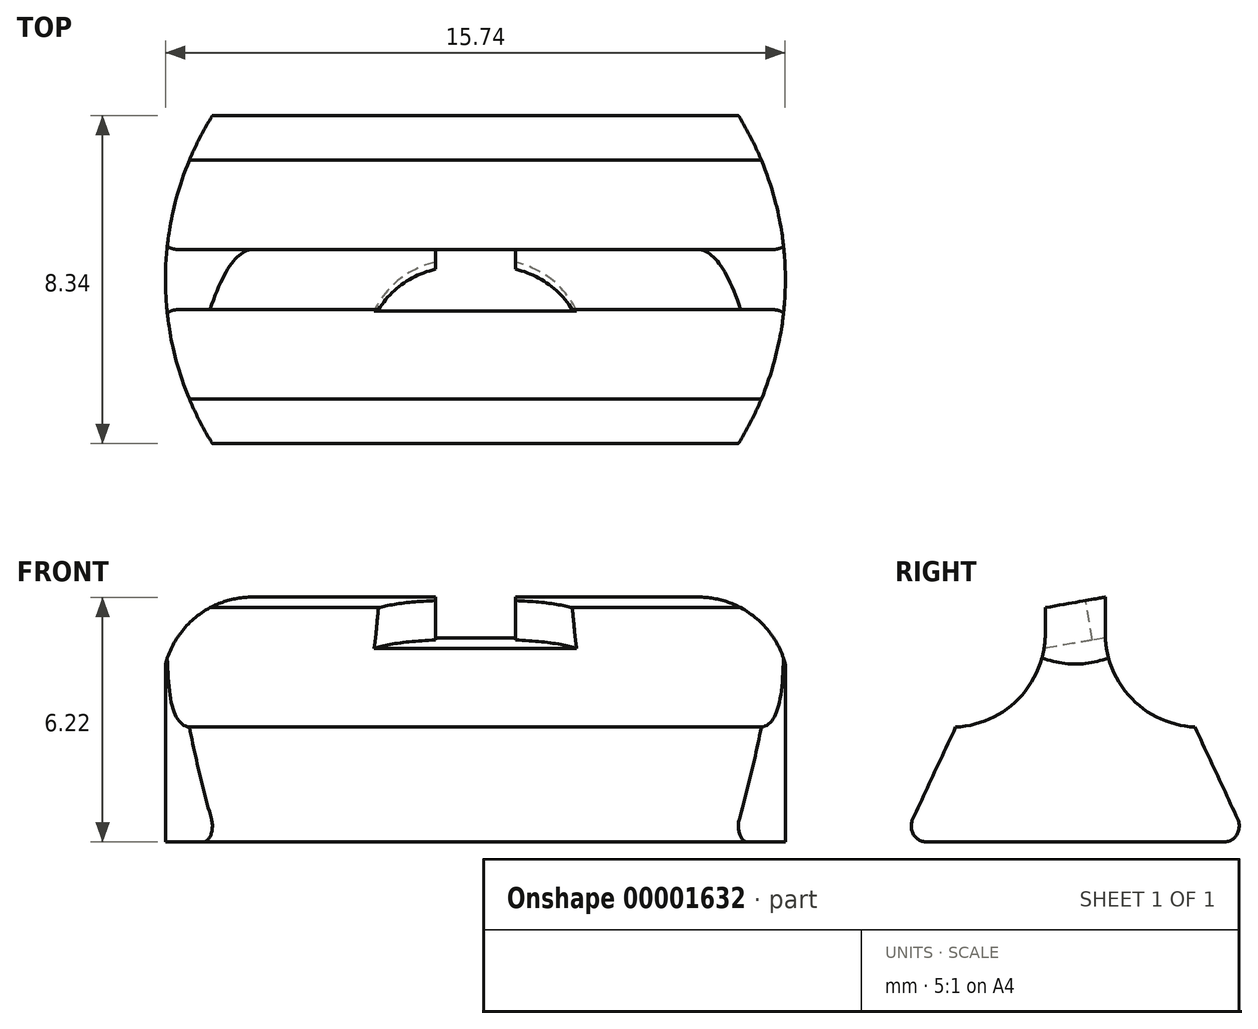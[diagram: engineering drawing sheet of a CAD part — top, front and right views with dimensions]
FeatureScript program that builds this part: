
annotation { "Feature Type Name" : "Feature", "Feature Type Description" : "" }
export const myFeature = defineFeature(function(context is Context, id is Id, definition is map)
    precondition{}
    {
        {
            var Q0;
            Q0=qCreatedBy(makeId("Right.planeOp"),FACE);
            var sketch = newSketch(context, id + "F0", { "sketchPlane" : qUnion([Q0])});
            skLineSegment(sketch, "E0", {"start": v(0, 0) * mm, "end": v(8.8, 0) * mm});
            skLineSegment(sketch, "E1", {"start": v(8.8, 0) * mm, "end": v(7.44, 2.92) * mm});
            skLineSegment(sketch, "E2", {"start": v(0, 0) * mm, "end": v(1.36, 2.92) * mm});
            skLineSegment(sketch, "E3", {"start": v(4.4, 0) * mm, "end": v(4.4, 6.09) * mm});
            skLineSegment(sketch, "E4", {"start": v(3.64, 5.95) * mm, "end": v(3.64, 5.3) * mm});
            skLineSegment(sketch, "E5", {"start": v(5.16, 6.22) * mm, "end": v(5.16, 5.3) * mm});
            skArc(sketch, "E6", {"start": v(1.36, 2.92) * mm, "mid": v(2.98, 3.66) * mm, "end": v(3.64, 5.3) * mm});
            skArc(sketch, "E7", {"start": v(5.16, 5.3) * mm, "mid": v(5.82, 3.66) * mm, "end": v(7.44, 2.92) * mm});
            skLineSegment(sketch, "E8", {"start": v(5.16, 6.22) * mm, "end": v(3.64, 5.95) * mm});
            skSolve(sketch);
        }
        {
            var Q0;
            {var subQ3=sQuery(id+"F0.wireOp",EDGE,"E2");Q0=makeQuery(id+"F0.imprint","IMPRINT",FACE,{"disambiguationData":[TD([[makeQuery(id+"F0.imprint","IMPRINT",EDGE,{"derivedFrom":subQ3}),-1.0]])]});}
            var Q1;
            {var subQ3=sQuery(id+"F0.wireOp",EDGE,"E1");Q1=makeQuery(id+"F0.imprint","IMPRINT",FACE,{"disambiguationData":[TD([[makeQuery(id+"F0.imprint","IMPRINT",EDGE,{"derivedFrom":subQ3}),1.0]])]});}
            extrude(context, id + "F1", {"entities" : qUnion([Q0, Q1]), "depth" : 15.9 * mm});
        }
        {
            var Q0;
            Q0=makeQuery(id+"F1.opExtrude","SWEPT_FACE",FACE,{"disambiguationData":[OSD([sQuery(id+"F0.wireOp",EDGE,"E8")])]});
            var sketch = newSketch(context, id + "F2", { "sketchPlane" : qUnion([Q0])});
            skLineSegment(sketch, "E9", {"start": v(7.95, 4.62) * mm, "end": v(7.95, 6.16) * mm, "construction": true});
            skLineSegment(sketch, "E10", {"start": v(8.97, 7.37) * mm, "end": v(8.97, 5.66) * mm});
            skLineSegment(sketch, "E11", {"start": v(6.93, 7.37) * mm, "end": v(6.93, 5.66) * mm});
            skLineSegment(sketch, "E12", {"start": v(8.97, 7.37) * mm, "end": v(6.93, 7.37) * mm});
            skLineSegment(sketch, "E13", {"start": v(7.44, 6.16) * mm, "end": v(7.44, 2.69) * mm, "construction": true});
            skLineSegment(sketch, "E14", {"start": v(8.46, 6.16) * mm, "end": v(8.46, 3.43) * mm, "construction": true});
            skArc(sketch, "E15", {"start": v(10.74, 3.54) * mm, "mid": v(10.2, 4.9) * mm, "end": v(8.97, 5.66) * mm});
            skPoint(sketch, "E16.orphan", {"position": v(0, 4.62) * mm});
            skArc(sketch, "E17.trimOffspring", {"start": v(6.93, 5.66) * mm, "mid": v(5.7, 4.9) * mm, "end": v(5.16, 3.54) * mm});
            skPoint(sketch, "E18.orphan", {"position": v(15.9, 4.62) * mm});
            skLineSegment(sketch, "E19", {"start": v(5.16, 3.54) * mm, "end": v(10.74, 3.54) * mm});
            skSolve(sketch);
        }
        {
            var Q0;
            {var subQ4=sQuery(id+"F2.wireOp",EDGE,"E10");var subQ9=sQuery(id+"F2.wireOp",EDGE,"E15");var subQ12=makeQuery(id+"F2.imprint","INTERSECT",VERTEX,{"derivedFrom":[subQ4,subQ9]});Q0=makeQuery(id+"F2.imprint","IMPRINT",FACE,{"disambiguationData":[TD([[makeQuery(id+"F2.imprint","IMPRINT",EDGE,{"disambiguationData":[TD([[subQ12,1.0]])],"derivedFrom":subQ4}),-1.0]])]});}
            var Q1;
            {var subQ5=sQuery(id+"F2.wireOp",EDGE,"E19");Q1=makeQuery(id+"F2.imprint","IMPRINT",FACE,{"disambiguationData":[TD([[makeQuery(id+"F2.imprint","IMPRINT",EDGE,{"derivedFrom":subQ5}),1.0]])]});}
            var Q2;
            {var subQ5=sQuery(id+"F2.wireOp",EDGE,"E12");Q2=makeQuery(id+"F2.imprint","IMPRINT",FACE,{"disambiguationData":[TD([[makeQuery(id+"F2.imprint","IMPRINT",EDGE,{"derivedFrom":subQ5}),1.0]])]});}
            extrude(context, id + "F3", {"entities" : qUnion([Q0, Q1, Q2]), "operationType" : NewBodyOperationType.REMOVE, "oppositeDirection" : true, "depth" : 1.02 * mm});
        }
        {
            var Q0;
            Q0=makeQuery(id+"F1.opExtrude","SWEPT_FACE",FACE,{"disambiguationData":[OSD([sQuery(id+"F0.wireOp",EDGE,"E0")])]});
            var sketch = newSketch(context, id + "F4", { "sketchPlane" : qUnion([Q0])});
            skPoint(sketch, "E20", {"position": v(7.95, -4.4) * mm});
            skCircle(sketch, "E21", {"center": v(7.95, -4.4) * mm, "radius": 7.87 * mm});
            skSolve(sketch);
        }
        {
            var Q0;
            {var subQ0=sQuery(id+"F0.wireOp",EDGE,"E0");var subQ4=makeQuery(id+"F1.opExtrude","CAP_EDGE",EDGE,{"disambiguationData":[OSD([subQ0])],"isStart":false});Q0=makeQuery(id+"F4.imprint","IMPRINT",FACE,{"disambiguationData":[TD([[makeQuery(id+"F4.imprint","IMPRINT",EDGE,{"derivedFrom":subQ4}),-1.0]])]});}
            var Q1;
            {var subQ0=sQuery(id+"F0.wireOp",EDGE,"E0");var subQ4=makeQuery(id+"F1.opExtrude","CAP_EDGE",EDGE,{"disambiguationData":[OSD([subQ0])],"isStart":true});Q1=makeQuery(id+"F4.imprint","IMPRINT",FACE,{"disambiguationData":[TD([[makeQuery(id+"F4.imprint","IMPRINT",EDGE,{"derivedFrom":subQ4}),1.0]])]});}
            extrude(context, id + "F5", {"entities" : qUnion([Q0, Q1]), "operationType" : NewBodyOperationType.REMOVE, "endBound" : BoundingType.THROUGH_ALL, "oppositeDirection" : true, "depth" : 25.4 * mm});
        }
        {
            var Q0;
            Q0=qCreatedBy(makeId("Front.planeOp"),FACE);
            var sketch = newSketch(context, id + "F6", { "sketchPlane" : qUnion([Q0])});
            skLineSegment(sketch, "E22.0", {"start": v(0, 6.22) * mm, "end": v(0, 5.95) * mm});
            skLineSegment(sketch, "E23.0", {"start": v(0, 5.95) * mm, "end": v(0, 5.3) * mm});
            skLineSegment(sketch, "E24.0", {"start": v(0, 5.3) * mm, "end": v(0, 2.92) * mm});
            skLineSegment(sketch, "E25.0", {"start": v(0, 0) * mm, "end": v(0, 2.92) * mm});
            skLineSegment(sketch, "E26.0", {"start": v(6.93, 6.22) * mm, "end": v(0, 6.22) * mm});
            skLineSegment(sketch, "E27.0", {"start": v(15.9, 0) * mm, "end": v(15.9, 2.92) * mm});
            skLineSegment(sketch, "E28.0", {"start": v(15.9, 5.3) * mm, "end": v(15.9, 2.92) * mm});
            skLineSegment(sketch, "E29.0", {"start": v(15.9, 5.95) * mm, "end": v(15.9, 5.3) * mm});
            skLineSegment(sketch, "E30.0", {"start": v(15.9, 6.22) * mm, "end": v(15.9, 5.95) * mm});
            skLineSegment(sketch, "E31.0", {"start": v(15.9, 6.22) * mm, "end": v(8.97, 6.22) * mm});
            skArc(sketch, "E32", {"start": v(2.29, 6.22) * mm, "mid": v(0.67, 5.55) * mm, "end": v(0, 3.94) * mm});
            skArc(sketch, "E33", {"start": v(15.9, 3.94) * mm, "mid": v(15.23, 5.55) * mm, "end": v(13.61, 6.22) * mm});
            skSolve(sketch);
        }
        {
            var Q0;
            {var subQ2=sQuery(id+"F6.wireOp",EDGE,"E22.0");Q0=makeQuery(id+"F6.imprint","IMPRINT",FACE,{"disambiguationData":[TD([[makeQuery(id+"F6.imprint","IMPRINT",EDGE,{"derivedFrom":subQ2}),1.0]])]});}
            var Q1;
            {var subQ3=sQuery(id+"F6.wireOp",EDGE,"E29.0");Q1=makeQuery(id+"F6.imprint","IMPRINT",FACE,{"disambiguationData":[TD([[makeQuery(id+"F6.imprint","IMPRINT",EDGE,{"derivedFrom":subQ3}),-1.0]])]});}
            extrude(context, id + "F7", {"entities" : qUnion([Q0, Q1]), "operationType" : NewBodyOperationType.REMOVE, "endBound" : BoundingType.SYMMETRIC, "oppositeDirection" : true, "depth" : 25.4 * mm});
        }
        {
            var Q0;
            Q0=makeQuery(id+"F1.opExtrude","SWEPT_EDGE",EDGE,{"disambiguationData":[OSD([sQuery(id+"F0.wireOp",EDGE,"E0"),sQuery(id+"F0.wireOp",EDGE,"E2")])]});
            var Q1;
            Q1=makeQuery(id+"F1.opExtrude","SWEPT_EDGE",EDGE,{"disambiguationData":[OSD([sQuery(id+"F0.wireOp",EDGE,"E0"),sQuery(id+"F0.wireOp",EDGE,"E1")])]});
            fillet(context, id + "F8", {"entities" : qUnion([Q0, Q1]), "radius" : 0.4 * mm, "tangentPropagation" : true, "allowEdgeOverflow" : false});
        }
    });
